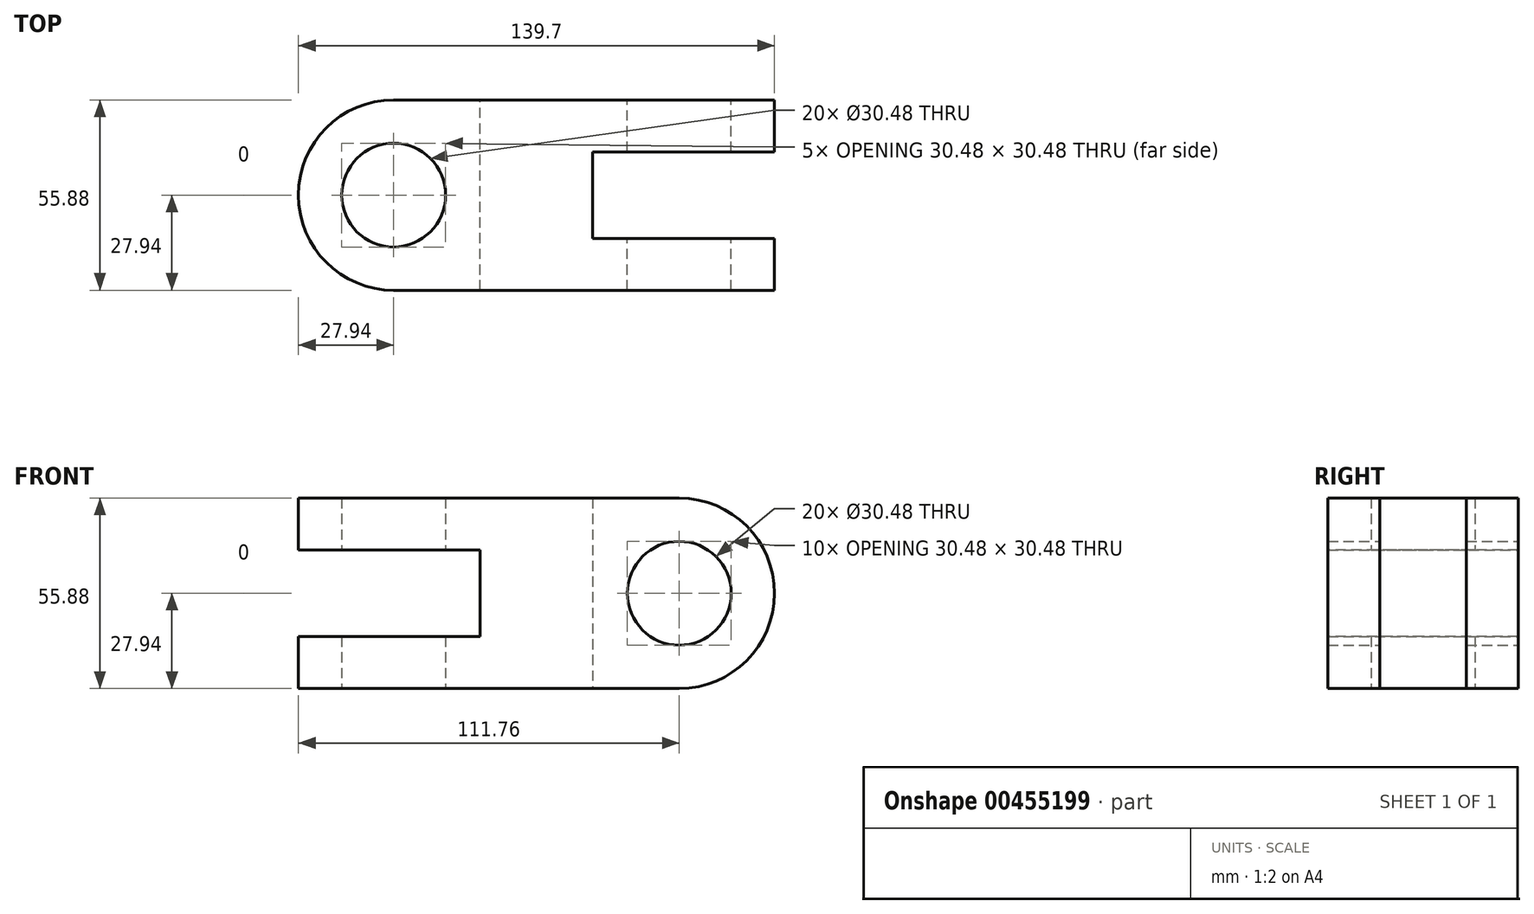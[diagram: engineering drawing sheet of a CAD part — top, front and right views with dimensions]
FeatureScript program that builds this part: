
annotation { "Feature Type Name" : "Feature", "Feature Type Description" : "" }
export const myFeature = defineFeature(function(context is Context, id is Id, definition is map)
    precondition{}
    {
        {
            var Q0;
            Q0=qCreatedBy(makeId("Top.planeOp"),FACE);
            var sketch = newSketch(context, id + "F0", { "sketchPlane" : qUnion([Q0])});
            skLineSegment(sketch, "E0.bottom", {"start": v(0, 0) * mm, "end": v(139.7, 0) * mm});
            skLineSegment(sketch, "E0.top", {"start": v(0, 55.88) * mm, "end": v(139.7, 55.88) * mm});
            skLineSegment(sketch, "E0.left", {"start": v(0, 0) * mm, "end": v(0, 55.88) * mm});
            skLineSegment(sketch, "E0.right", {"start": v(139.7, 0) * mm, "end": v(139.7, 55.88) * mm});
            skSolve(sketch);
        }
        {
            var Q0;
            Q0 = qSketchRegion(id + "F0", true);
            extrude(context, id + "F1", {"entities" : qUnion([Q0]), "depth" : 55.88 * mm});
        }
        {
            var Q0;
            Q0=makeQuery(id+"F1.opExtrude","CAP_FACE",FACE,{"disambiguationData":[OSD([sQuery(id+"F0.wireOp",EDGE,"E0.bottom"),sQuery(id+"F0.wireOp",EDGE,"E0.top"),sQuery(id+"F0.wireOp",EDGE,"E0.left"),sQuery(id+"F0.wireOp",EDGE,"E0.right")])],"isStart":true});
            var sketch = newSketch(context, id + "F2", { "sketchPlane" : qUnion([Q0])});
            skLineSegment(sketch, "E1.bottom", {"start": v(187.96, -15.24) * mm, "end": v(86.36, -15.24) * mm});
            skLineSegment(sketch, "E1.top", {"start": v(187.96, -40.64) * mm, "end": v(86.36, -40.64) * mm});
            skLineSegment(sketch, "E1.left", {"start": v(187.96, -15.24) * mm, "end": v(187.96, -40.64) * mm});
            skLineSegment(sketch, "E1.right", {"start": v(86.36, -15.24) * mm, "end": v(86.36, -40.64) * mm});
            skSolve(sketch);
        }
        {
            var Q0;
            Q0 = qSketchRegion(id + "F2", true);
            extrude(context, id + "F3", {"entities" : qUnion([Q0]), "operationType" : NewBodyOperationType.REMOVE, "endBound" : BoundingType.THROUGH_ALL, "oppositeDirection" : true, "depth" : 50.8 * mm});
        }
        {
            var Q0;
            {var subQ0=sQuery(id+"F0.wireOp",EDGE,"E0.right");var subQ1=sQuery(id+"F0.wireOp",EDGE,"E0.top");Q0=makeQuery(id+"F3.boolean.opBoolean","SPLIT",EDGE,{"disambiguationData":[TD([makeQuery(id+"F1.opExtrude","SWEPT_FACE",FACE,{"disambiguationData":[OSD([subQ1])]})])],"derivedFrom":makeQuery(id+"F1.opExtrude","CAP_EDGE",EDGE,{"disambiguationData":[OSD([subQ0])],"isStart":false})});}
            var Q1;
            {var subQ0=sQuery(id+"F0.wireOp",EDGE,"E0.bottom");var subQ1=sQuery(id+"F0.wireOp",EDGE,"E0.right");Q1=makeQuery(id+"F3.boolean.opBoolean","SPLIT",EDGE,{"disambiguationData":[TD([makeQuery(id+"F1.opExtrude","SWEPT_FACE",FACE,{"disambiguationData":[OSD([subQ0])]})])],"derivedFrom":makeQuery(id+"F1.opExtrude","CAP_EDGE",EDGE,{"disambiguationData":[OSD([subQ1])],"isStart":false})});}
            var Q2;
            {var subQ0=sQuery(id+"F0.wireOp",EDGE,"E0.bottom");var subQ1=sQuery(id+"F0.wireOp",EDGE,"E0.right");Q2=makeQuery(id+"F3.boolean.opBoolean","SPLIT",EDGE,{"disambiguationData":[TD([makeQuery(id+"F1.opExtrude","SWEPT_FACE",FACE,{"disambiguationData":[OSD([subQ0])]})])],"derivedFrom":makeQuery(id+"F1.opExtrude","CAP_EDGE",EDGE,{"disambiguationData":[OSD([subQ1])],"isStart":true})});}
            var Q3;
            {var subQ0=sQuery(id+"F0.wireOp",EDGE,"E0.right");var subQ1=sQuery(id+"F0.wireOp",EDGE,"E0.top");Q3=makeQuery(id+"F3.boolean.opBoolean","SPLIT",EDGE,{"disambiguationData":[TD([makeQuery(id+"F1.opExtrude","SWEPT_FACE",FACE,{"disambiguationData":[OSD([subQ1])]})])],"derivedFrom":makeQuery(id+"F1.opExtrude","CAP_EDGE",EDGE,{"disambiguationData":[OSD([subQ0])],"isStart":true})});}
            var Q4;
            Q4=makeQuery(id+"F1.opExtrude","SWEPT_EDGE",EDGE,{"disambiguationData":[OSD([sQuery(id+"F0.wireOp",EDGE,"E0.top"),sQuery(id+"F0.wireOp",EDGE,"E0.left")])]});
            var Q5;
            Q5=makeQuery(id+"F1.opExtrude","SWEPT_EDGE",EDGE,{"disambiguationData":[OSD([sQuery(id+"F0.wireOp",EDGE,"E0.bottom"),sQuery(id+"F0.wireOp",EDGE,"E0.left")])]});
            fillet(context, id + "F4", {"entities" : qUnion([Q0, Q1, Q2, Q3, Q4, Q5]), "radius" : 27.94 * mm, "tangentPropagation" : true, "allowEdgeOverflow" : false});
        }
        {
            var Q0;
            Q0=makeQuery(id+"F1.opExtrude","SWEPT_FACE",FACE,{"disambiguationData":[OSD([sQuery(id+"F0.wireOp",EDGE,"E0.top")])]});
            var sketch = newSketch(context, id + "F5", { "sketchPlane" : qUnion([Q0])});
            skCircle(sketch, "E2", {"center": v(-111.76, 27.94) * mm, "radius": 15.24 * mm});
            skSolve(sketch);
        }
        {
            var Q0;
            Q0=makeQuery(id+"F5.imprint","IMPRINT",FACE,{"disambiguationData":[TD([[makeQuery(id+"F5.imprint","IMPRINT",EDGE,{"derivedFrom":sQuery(id+"F5.wireOp",EDGE,"E2")}),1.0]])]});
            extrude(context, id + "F6", {"entities" : qUnion([Q0]), "operationType" : NewBodyOperationType.REMOVE, "endBound" : BoundingType.THROUGH_ALL, "oppositeDirection" : true, "depth" : 25.4 * mm});
        }
        {
            var Q0;
            Q0=makeQuery(id+"F1.opExtrude","SWEPT_FACE",FACE,{"disambiguationData":[OSD([sQuery(id+"F0.wireOp",EDGE,"E0.top")])]});
            var sketch = newSketch(context, id + "F7", { "sketchPlane" : qUnion([Q0])});
            skLineSegment(sketch, "E3.bottom", {"start": v(22.86, 40.64) * mm, "end": v(-53.34, 40.64) * mm});
            skLineSegment(sketch, "E3.top", {"start": v(22.86, 15.24) * mm, "end": v(-53.34, 15.24) * mm});
            skLineSegment(sketch, "E3.left", {"start": v(22.86, 40.64) * mm, "end": v(22.86, 15.24) * mm});
            skLineSegment(sketch, "E3.right", {"start": v(-53.34, 40.64) * mm, "end": v(-53.34, 15.24) * mm});
            skSolve(sketch);
        }
        {
            var Q0;
            Q0 = qSketchRegion(id + "F7", true);
            extrude(context, id + "F8", {"entities" : qUnion([Q0]), "operationType" : NewBodyOperationType.REMOVE, "endBound" : BoundingType.THROUGH_ALL, "oppositeDirection" : true, "depth" : 25.4 * mm});
        }
        {
            var Q0;
            Q0=makeQuery(id+"F1.opExtrude","CAP_FACE",FACE,{"disambiguationData":[OSD([sQuery(id+"F0.wireOp",EDGE,"E0.bottom"),sQuery(id+"F0.wireOp",EDGE,"E0.top"),sQuery(id+"F0.wireOp",EDGE,"E0.left"),sQuery(id+"F0.wireOp",EDGE,"E0.right")])],"isStart":true});
            var sketch = newSketch(context, id + "F9", { "sketchPlane" : qUnion([Q0])});
            skCircle(sketch, "E4", {"center": v(27.94, -27.94) * mm, "radius": 15.24 * mm});
            skSolve(sketch);
        }
        {
            var Q0;
            Q0 = qSketchRegion(id + "F9", true);
            extrude(context, id + "F10", {"entities" : qUnion([Q0]), "operationType" : NewBodyOperationType.REMOVE, "endBound" : BoundingType.THROUGH_ALL, "oppositeDirection" : true, "depth" : 25.4 * mm});
        }
    });
